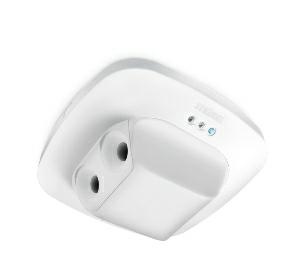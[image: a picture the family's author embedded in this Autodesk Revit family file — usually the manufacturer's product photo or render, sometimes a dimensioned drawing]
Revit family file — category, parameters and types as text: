
# Revit family: dual_us_059491
name_source: partatom
category: Elektroinstallationen
revit_build: Autodesk Revit 2016 (Build: 20190508_0715(x64)
units: mm (PartAtom-declared; Revit-internal decimal feet)

## family parameters
Basisbauteil = Fläche
Beim Laden mit Abzugskörper schneiden = Nein
Bemaßung runder Anschluss = Durchmesser verwenden
Beschriftungsausrichtung beibehalten = Nein
Gemeinsam genutzt = Nein
Raumberechnungspunkt = Nein
Teiletyp = Normal

## types (1)
- Dual US
    Apparent Load = 0 VA
    Beschreibung = Type: Presence detector; Dimensions (L x W x H): 73 x 120 x 120 mm; Mains power supply: 30 V; Power consumption: 0,7 W; Sensor Technology: Ultrasonic; Application, place: Indoors; Application, room: corridor / aisle, Indoors; Installation site: ceiling; Installation: Concealed wiring; Electronic scalability: Yes; Mechanical scalability: No; Mounting height: 2,50 – 3,5 m; Optimum mounting height: 2,8 m; Detection angle: 360 °; Angle of aperture: 160 °; Sneak-by guard: Yes; Capability of masking out individual segments: No; Twilight setting TEACH: Yes; Twilight setting: 10 – 1000 lx; Time setting: 0 sec – 1092 min; Constant-lighting control: Yes; Basic light level function: Yes; Basic light level function time: 1-255 min; KNX functions: Photo-cell controller, Basic light level function, Light level, HVAC output, Constant-lighting control, Light output 4x, Presence output, Day / night function; With bus coupling: Yes; Settings via: ETS software, Remote control, Bus, Smart Remote; With remote control: Yes; Interconnection: Yes; IP-rating: IP20; Material: Plastic; Ambient temperature: -25 – 55 °C; Colour: white; Colour, RAL: 9010; Manufacturer's Warranty: 5 years; Version: KNX; PU1, EAN: 4007841059491
    Height = 0 mm  [stored 0 ft]
    Hersteller = Steinel
    Length = 73 mm
    Maximum range = 10.098 m
    ModVariant = Nein
    Modell = 059491
    Mounting Place = Ceiling
    Mounting Type = Recessed
    Number of Poles = 1
    OnlyDefault = Ja
    Power Factor = 1
    Product Name = Dual US
    Product group = Presence detector
    ProductGroupID = 4
    Protection Class = Protection class
    Protection Degree = IP 20
    RlxData = <blob elided: 160765 chars, md5=eab4237e>
    Sensor characteristics = Stretched
    Sensor type = Passive (infrared)
    SensorDataFile = <blob elided: 184890 chars, md5=e609621d>
    Type of entry = Motion
    Typenbild = produkt1_059491.jpg
    Typenkommentare = Product without accessories
    URL = http://relux.com
    VarID = ---
    Voltage = 0 V
    Vorgabe-Ansicht = 1800 mm
    Weight = 0.00 kg
    Width = 120 mm  [stored 0.393701 ft]

note: [stored X ft] marks values corroborated as IEEE doubles in the binary element streams (Revit-internal decimal feet)

## geometry (parser evidence)
native form markers: Sweep x14
no freeform markers — native parametric forms only
